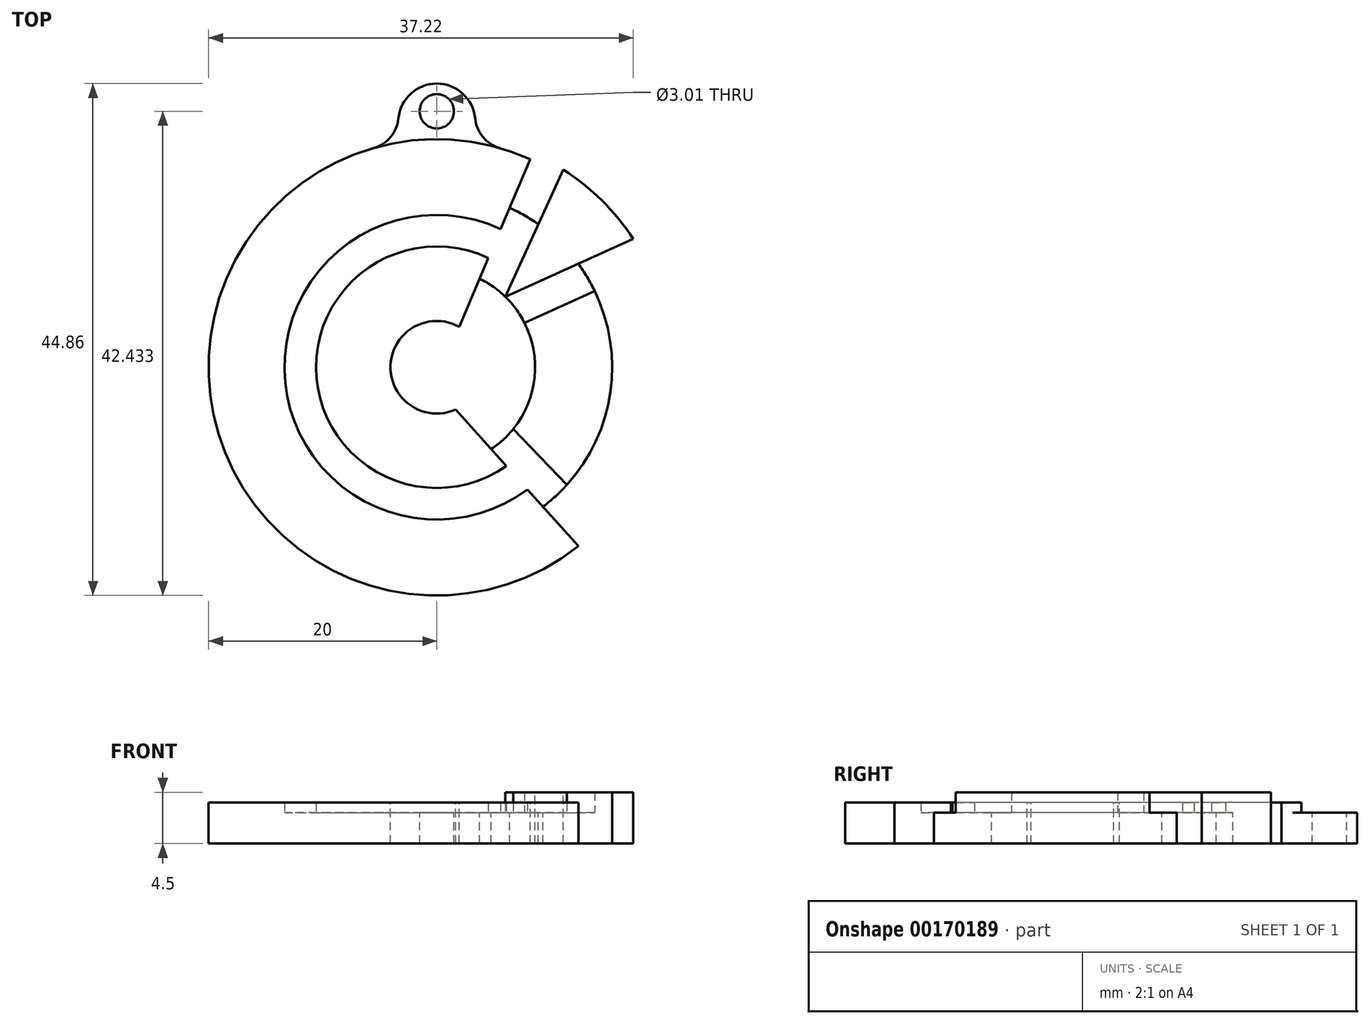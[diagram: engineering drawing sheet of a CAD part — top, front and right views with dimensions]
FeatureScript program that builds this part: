
annotation { "Feature Type Name" : "Feature", "Feature Type Description" : "" }
export const myFeature = defineFeature(function(context is Context, id is Id, definition is map)
    precondition{}
    {
        {
            var Q0;
            Q0=qCreatedBy(makeId("Top.planeOp"),FACE);
            var sketch = newSketch(context, id + "F0", { "sketchPlane" : qUnion([Q0])});
            skCircle(sketch, "E0", {"center": v(0, 0) * mm, "radius": 20 * mm});
            skCircle(sketch, "E1", {"center": v(0, 0) * mm, "radius": 13.35 * mm});
            skCircle(sketch, "E2", {"center": v(0, 0) * mm, "radius": 4.06 * mm});
            skCircle(sketch, "E3", {"center": v(0, 0) * mm, "radius": 10.58 * mm});
            skCircle(sketch, "E4", {"center": v(0, 0) * mm, "radius": 8.61 * mm});
            skCircle(sketch, "E5", {"center": v(0, 0) * mm, "radius": 15.36 * mm});
            skCircle(sketch, "E6", {"center": v(0, 0) * mm, "radius": 20.56 * mm});
            skCircle(sketch, "E7", {"center": v(0, 21.5) * mm, "radius": 3.37 * mm});
            skCircle(sketch, "E8", {"center": v(0, 22.43) * mm, "radius": 1.5 * mm});
            skLineSegment(sketch, "E9", {"start": v(6, 6.18) * mm, "end": v(11.07, 17.32) * mm});
            skLineSegment(sketch, "E10", {"start": v(6, 6.18) * mm, "end": v(17.22, 11.24) * mm});
            skLineSegment(sketch, "E11", {"start": v(8.19, 18.25) * mm, "end": v(1.98, 3.54) * mm});
            skLineSegment(sketch, "E12", {"start": v(1.66, -3.7) * mm, "end": v(12.41, -15.68) * mm});
            skLineSegment(sketch, "E13", {"start": v(7.68, 3.9) * mm, "end": v(13.83, 6.68) * mm});
            skLineSegment(sketch, "E14", {"start": v(11.4, -10.3) * mm, "end": v(6.71, -5.4) * mm});
            skSolve(sketch);
        }
        {
            var Q0;
            {var subQ1=sQuery(id+"F0.wireOp",EDGE,"E0");var subQ4=sQuery(id+"F0.wireOp",EDGE,"E11");var subQ10=makeQuery(id+"F0.imprint","INTERSECT",VERTEX,{"derivedFrom":[subQ1,subQ4]});Q0=makeQuery(id+"F0.imprint","IMPRINT",FACE,{"disambiguationData":[TD([[makeQuery(id+"F0.imprint","IMPRINT",EDGE,{"disambiguationData":[TD([[subQ10,-1.0]])],"derivedFrom":subQ1}),1.0]])]});}
            var Q1;
            {var subQ0=sQuery(id+"F0.wireOp",EDGE,"E11");var subQ1=sQuery(id+"F0.wireOp",EDGE,"E1");var subQ2=makeQuery(id+"F0.imprint","INTERSECT",VERTEX,{"derivedFrom":[subQ1,subQ0]});Q1=makeQuery(id+"F0.imprint","IMPRINT",FACE,{"disambiguationData":[TD([[makeQuery(id+"F0.imprint","IMPRINT",EDGE,{"disambiguationData":[TD([[subQ2,-1.0]])],"derivedFrom":subQ1}),-1.0]])]});}
            var Q2;
            {var subQ0=sQuery(id+"F0.wireOp",EDGE,"E11");var subQ1=sQuery(id+"F0.wireOp",EDGE,"E1");var subQ2=makeQuery(id+"F0.imprint","INTERSECT",VERTEX,{"derivedFrom":[subQ1,subQ0]});Q2=makeQuery(id+"F0.imprint","IMPRINT",FACE,{"disambiguationData":[TD([[makeQuery(id+"F0.imprint","IMPRINT",EDGE,{"disambiguationData":[TD([[subQ2,-1.0]])],"derivedFrom":subQ1}),1.0]])]});}
            var Q3;
            {var subQ0=sQuery(id+"F0.wireOp",EDGE,"E11");var subQ1=sQuery(id+"F0.wireOp",EDGE,"E3");var subQ2=makeQuery(id+"F0.imprint","INTERSECT",VERTEX,{"derivedFrom":[subQ1,subQ0]});Q3=makeQuery(id+"F0.imprint","IMPRINT",FACE,{"disambiguationData":[TD([[makeQuery(id+"F0.imprint","IMPRINT",EDGE,{"disambiguationData":[TD([[subQ2,-1.0]])],"derivedFrom":subQ1}),1.0]])]});}
            var Q4;
            {var subQ0=sQuery(id+"F0.wireOp",EDGE,"E11");var subQ1=sQuery(id+"F0.wireOp",EDGE,"E2");var subQ2=makeQuery(id+"F0.imprint","INTERSECT",VERTEX,{"derivedFrom":[subQ1,subQ0]});Q4=makeQuery(id+"F0.imprint","IMPRINT",FACE,{"disambiguationData":[TD([[makeQuery(id+"F0.imprint","IMPRINT",EDGE,{"disambiguationData":[TD([[subQ2,-1.0]])],"derivedFrom":subQ1}),-1.0]])]});}
            var Q5;
            {var subQ0=sQuery(id+"F0.wireOp",EDGE,"E7");var subQ1=sQuery(id+"F0.wireOp",EDGE,"E0");var subQ2=makeQuery(id+"F0.imprint","INTERSECT",VERTEX,{"disambiguationData":[OD(0.0)],"derivedFrom":[subQ1,subQ0]});Q5=makeQuery(id+"F0.imprint","IMPRINT",FACE,{"disambiguationData":[TD([[makeQuery(id+"F0.imprint","IMPRINT",EDGE,{"disambiguationData":[TD([[subQ2,-1.0]])],"derivedFrom":subQ1}),1.0]])]});}
            var Q6;
            {var subQ0=sQuery(id+"F0.wireOp",EDGE,"E7");var subQ1=sQuery(id+"F0.wireOp",EDGE,"E0");var subQ2=makeQuery(id+"F0.imprint","INTERSECT",VERTEX,{"disambiguationData":[OD(0.0)],"derivedFrom":[subQ1,subQ0]});Q6=makeQuery(id+"F0.imprint","IMPRINT",FACE,{"disambiguationData":[TD([[makeQuery(id+"F0.imprint","IMPRINT",EDGE,{"disambiguationData":[TD([[subQ2,-1.0]])],"derivedFrom":subQ1}),-1.0]])]});}
            var Q7;
            Q7=makeQuery(id+"F0.imprint","IMPRINT",FACE,{"disambiguationData":[TD([[makeQuery(id+"F0.imprint","IMPRINT",EDGE,{"derivedFrom":sQuery(id+"F0.wireOp",EDGE,"E8")}),-1.0]])]});
            var Q8;
            {var subQ0=sQuery(id+"F0.wireOp",EDGE,"E10");var subQ1=sQuery(id+"F0.wireOp",EDGE,"E1");var subQ2=makeQuery(id+"F0.imprint","INTERSECT",VERTEX,{"derivedFrom":[subQ1,subQ0]});Q8=makeQuery(id+"F0.imprint","IMPRINT",FACE,{"disambiguationData":[TD([[makeQuery(id+"F0.imprint","IMPRINT",EDGE,{"disambiguationData":[TD([[subQ2,1.0]])],"derivedFrom":subQ1}),-1.0]])]});}
            var Q9;
            {var subQ0=sQuery(id+"F0.wireOp",EDGE,"E10");var subQ1=sQuery(id+"F0.wireOp",EDGE,"E1");var subQ2=makeQuery(id+"F0.imprint","INTERSECT",VERTEX,{"derivedFrom":[subQ1,subQ0]});Q9=makeQuery(id+"F0.imprint","IMPRINT",FACE,{"disambiguationData":[TD([[makeQuery(id+"F0.imprint","IMPRINT",EDGE,{"disambiguationData":[TD([[subQ2,1.0]])],"derivedFrom":subQ1}),1.0]])]});}
            var Q10;
            {var subQ0=sQuery(id+"F0.wireOp",EDGE,"E10");var subQ1=sQuery(id+"F0.wireOp",EDGE,"E3");var subQ2=makeQuery(id+"F0.imprint","INTERSECT",VERTEX,{"derivedFrom":[subQ1,subQ0]});Q10=makeQuery(id+"F0.imprint","IMPRINT",FACE,{"disambiguationData":[TD([[makeQuery(id+"F0.imprint","IMPRINT",EDGE,{"disambiguationData":[TD([[subQ2,1.0]])],"derivedFrom":subQ1}),1.0]])]});}
            var Q11;
            {var subQ0=sQuery(id+"F0.wireOp",EDGE,"E9");var subQ1=sQuery(id+"F0.wireOp",EDGE,"E3");var subQ2=makeQuery(id+"F0.imprint","INTERSECT",VERTEX,{"derivedFrom":[subQ1,subQ0]});Q11=makeQuery(id+"F0.imprint","IMPRINT",FACE,{"disambiguationData":[TD([[makeQuery(id+"F0.imprint","IMPRINT",EDGE,{"disambiguationData":[TD([[subQ2,1.0]])],"derivedFrom":subQ1}),1.0]])]});}
            var Q12;
            {var subQ0=sQuery(id+"F0.wireOp",EDGE,"E9");var subQ1=sQuery(id+"F0.wireOp",EDGE,"E3");var subQ2=makeQuery(id+"F0.imprint","INTERSECT",VERTEX,{"derivedFrom":[subQ1,subQ0]});Q12=makeQuery(id+"F0.imprint","IMPRINT",FACE,{"disambiguationData":[TD([[makeQuery(id+"F0.imprint","IMPRINT",EDGE,{"disambiguationData":[TD([[subQ2,-1.0]])],"derivedFrom":subQ1}),1.0]])]});}
            var Q13;
            {var subQ0=sQuery(id+"F0.wireOp",EDGE,"E9");var subQ1=sQuery(id+"F0.wireOp",EDGE,"E1");var subQ2=makeQuery(id+"F0.imprint","INTERSECT",VERTEX,{"derivedFrom":[subQ1,subQ0]});Q13=makeQuery(id+"F0.imprint","IMPRINT",FACE,{"disambiguationData":[TD([[makeQuery(id+"F0.imprint","IMPRINT",EDGE,{"disambiguationData":[TD([[subQ2,-1.0]])],"derivedFrom":subQ1}),1.0]])]});}
            var Q14;
            {var subQ0=sQuery(id+"F0.wireOp",EDGE,"E9");var subQ1=sQuery(id+"F0.wireOp",EDGE,"E1");var subQ2=makeQuery(id+"F0.imprint","INTERSECT",VERTEX,{"derivedFrom":[subQ1,subQ0]});Q14=makeQuery(id+"F0.imprint","IMPRINT",FACE,{"disambiguationData":[TD([[makeQuery(id+"F0.imprint","IMPRINT",EDGE,{"disambiguationData":[TD([[subQ2,-1.0]])],"derivedFrom":subQ1}),-1.0]])]});}
            var Q15;
            {var subQ0=sQuery(id+"F0.wireOp",EDGE,"E9");var subQ1=sQuery(id+"F0.wireOp",EDGE,"E1");var subQ2=makeQuery(id+"F0.imprint","INTERSECT",VERTEX,{"derivedFrom":[subQ1,subQ0]});Q15=makeQuery(id+"F0.imprint","IMPRINT",FACE,{"disambiguationData":[TD([[makeQuery(id+"F0.imprint","IMPRINT",EDGE,{"disambiguationData":[TD([[subQ2,1.0]])],"derivedFrom":subQ1}),1.0]])]});}
            var Q16;
            {var subQ0=sQuery(id+"F0.wireOp",EDGE,"E9");var subQ1=sQuery(id+"F0.wireOp",EDGE,"E1");var subQ2=makeQuery(id+"F0.imprint","INTERSECT",VERTEX,{"derivedFrom":[subQ1,subQ0]});Q16=makeQuery(id+"F0.imprint","IMPRINT",FACE,{"disambiguationData":[TD([[makeQuery(id+"F0.imprint","IMPRINT",EDGE,{"disambiguationData":[TD([[subQ2,1.0]])],"derivedFrom":subQ1}),-1.0]])]});}
            var Q17;
            {var subQ0=sQuery(id+"F0.wireOp",EDGE,"E9");var subQ1=sQuery(id+"F0.wireOp",EDGE,"E0");var subQ2=makeQuery(id+"F0.imprint","INTERSECT",VERTEX,{"derivedFrom":[subQ1,subQ0]});Q17=makeQuery(id+"F0.imprint","IMPRINT",FACE,{"disambiguationData":[TD([[makeQuery(id+"F0.imprint","IMPRINT",EDGE,{"disambiguationData":[TD([[subQ2,1.0]])],"derivedFrom":subQ1}),1.0]])]});}
            var Q18;
            {var subQ0=sQuery(id+"F0.wireOp",EDGE,"E9");var subQ1=sQuery(id+"F0.wireOp",EDGE,"E0");var subQ2=makeQuery(id+"F0.imprint","INTERSECT",VERTEX,{"derivedFrom":[subQ1,subQ0]});Q18=makeQuery(id+"F0.imprint","IMPRINT",FACE,{"disambiguationData":[TD([[makeQuery(id+"F0.imprint","IMPRINT",EDGE,{"disambiguationData":[TD([[subQ2,1.0]])],"derivedFrom":subQ1}),-1.0]])]});}
            extrude(context, id + "F1", {"entities" : qUnion([Q0, Q1, Q2, Q3, Q4, Q5, Q6, Q7, Q8, Q9, Q10, Q11, Q12, Q13, Q14, Q15, Q16, Q17, Q18]), "oppositeDirection" : true, "depth" : 2.7 * mm});
        }
        {
            var Q0;
            {var subQ1=sQuery(id+"F0.wireOp",EDGE,"E0");var subQ4=sQuery(id+"F0.wireOp",EDGE,"E11");var subQ10=makeQuery(id+"F0.imprint","INTERSECT",VERTEX,{"derivedFrom":[subQ1,subQ4]});Q0=makeQuery(id+"F0.imprint","IMPRINT",FACE,{"disambiguationData":[TD([[makeQuery(id+"F0.imprint","IMPRINT",EDGE,{"disambiguationData":[TD([[subQ10,-1.0]])],"derivedFrom":subQ1}),1.0]])]});}
            var Q1;
            {var subQ0=sQuery(id+"F0.wireOp",EDGE,"E11");var subQ1=sQuery(id+"F0.wireOp",EDGE,"E1");var subQ2=makeQuery(id+"F0.imprint","INTERSECT",VERTEX,{"derivedFrom":[subQ1,subQ0]});Q1=makeQuery(id+"F0.imprint","IMPRINT",FACE,{"disambiguationData":[TD([[makeQuery(id+"F0.imprint","IMPRINT",EDGE,{"disambiguationData":[TD([[subQ2,-1.0]])],"derivedFrom":subQ1}),-1.0]])]});}
            var Q2;
            {var subQ0=sQuery(id+"F0.wireOp",EDGE,"E11");var subQ1=sQuery(id+"F0.wireOp",EDGE,"E3");var subQ2=makeQuery(id+"F0.imprint","INTERSECT",VERTEX,{"derivedFrom":[subQ1,subQ0]});Q2=makeQuery(id+"F0.imprint","IMPRINT",FACE,{"disambiguationData":[TD([[makeQuery(id+"F0.imprint","IMPRINT",EDGE,{"disambiguationData":[TD([[subQ2,-1.0]])],"derivedFrom":subQ1}),1.0]])]});}
            var Q3;
            {var subQ0=sQuery(id+"F0.wireOp",EDGE,"E11");var subQ1=sQuery(id+"F0.wireOp",EDGE,"E2");var subQ2=makeQuery(id+"F0.imprint","INTERSECT",VERTEX,{"derivedFrom":[subQ1,subQ0]});Q3=makeQuery(id+"F0.imprint","IMPRINT",FACE,{"disambiguationData":[TD([[makeQuery(id+"F0.imprint","IMPRINT",EDGE,{"disambiguationData":[TD([[subQ2,-1.0]])],"derivedFrom":subQ1}),-1.0]])]});}
            var Q4;
            {var subQ0=sQuery(id+"F0.wireOp",EDGE,"E7");var subQ1=sQuery(id+"F0.wireOp",EDGE,"E0");var subQ2=makeQuery(id+"F0.imprint","INTERSECT",VERTEX,{"disambiguationData":[OD(0.0)],"derivedFrom":[subQ1,subQ0]});Q4=makeQuery(id+"F0.imprint","IMPRINT",FACE,{"disambiguationData":[TD([[makeQuery(id+"F0.imprint","IMPRINT",EDGE,{"disambiguationData":[TD([[subQ2,-1.0]])],"derivedFrom":subQ1}),1.0]])]});}
            extrude(context, id + "F2", {"entities" : qUnion([Q0, Q1, Q2, Q3, Q4]), "operationType" : NewBodyOperationType.ADD, "depth" : 0.9 * mm});
        }
        {
            var Q0;
            {var subQ0=sQuery(id+"F0.wireOp",EDGE,"E13");var subQ1=sQuery(id+"F0.wireOp",EDGE,"E3");var subQ2=makeQuery(id+"F0.imprint","INTERSECT",VERTEX,{"derivedFrom":[subQ1,subQ0]});Q0=makeQuery(id+"F0.imprint","IMPRINT",FACE,{"disambiguationData":[TD([[makeQuery(id+"F0.imprint","IMPRINT",EDGE,{"disambiguationData":[TD([[subQ2,1.0]])],"derivedFrom":subQ1}),1.0]])]});}
            var Q1;
            {var subQ0=sQuery(id+"F0.wireOp",EDGE,"E13");var subQ1=sQuery(id+"F0.wireOp",EDGE,"E1");var subQ2=makeQuery(id+"F0.imprint","INTERSECT",VERTEX,{"derivedFrom":[subQ1,subQ0]});Q1=makeQuery(id+"F0.imprint","IMPRINT",FACE,{"disambiguationData":[TD([[makeQuery(id+"F0.imprint","IMPRINT",EDGE,{"disambiguationData":[TD([[subQ2,1.0]])],"derivedFrom":subQ1}),1.0]])]});}
            var Q2;
            {var subQ0=sQuery(id+"F0.wireOp",EDGE,"E13");var subQ1=sQuery(id+"F0.wireOp",EDGE,"E1");var subQ2=makeQuery(id+"F0.imprint","INTERSECT",VERTEX,{"derivedFrom":[subQ1,subQ0]});Q2=makeQuery(id+"F0.imprint","IMPRINT",FACE,{"disambiguationData":[TD([[makeQuery(id+"F0.imprint","IMPRINT",EDGE,{"disambiguationData":[TD([[subQ2,1.0]])],"derivedFrom":subQ1}),-1.0]])]});}
            var Q3;
            {var subQ0=sQuery(id+"F0.wireOp",EDGE,"E12");var subQ1=sQuery(id+"F0.wireOp",EDGE,"E1");var subQ2=makeQuery(id+"F0.imprint","INTERSECT",VERTEX,{"derivedFrom":[subQ1,subQ0]});Q3=makeQuery(id+"F0.imprint","IMPRINT",FACE,{"disambiguationData":[TD([[makeQuery(id+"F0.imprint","IMPRINT",EDGE,{"disambiguationData":[TD([[subQ2,-1.0]])],"derivedFrom":subQ1}),-1.0]])]});}
            var Q4;
            {var subQ0=sQuery(id+"F0.wireOp",EDGE,"E12");var subQ1=sQuery(id+"F0.wireOp",EDGE,"E1");var subQ2=makeQuery(id+"F0.imprint","INTERSECT",VERTEX,{"derivedFrom":[subQ1,subQ0]});Q4=makeQuery(id+"F0.imprint","IMPRINT",FACE,{"disambiguationData":[TD([[makeQuery(id+"F0.imprint","IMPRINT",EDGE,{"disambiguationData":[TD([[subQ2,-1.0]])],"derivedFrom":subQ1}),1.0]])]});}
            var Q5;
            {var subQ0=sQuery(id+"F0.wireOp",EDGE,"E12");var subQ1=sQuery(id+"F0.wireOp",EDGE,"E3");var subQ2=makeQuery(id+"F0.imprint","INTERSECT",VERTEX,{"derivedFrom":[subQ1,subQ0]});Q5=makeQuery(id+"F0.imprint","IMPRINT",FACE,{"disambiguationData":[TD([[makeQuery(id+"F0.imprint","IMPRINT",EDGE,{"disambiguationData":[TD([[subQ2,-1.0]])],"derivedFrom":subQ1}),1.0]])]});}
            extrude(context, id + "F3", {"entities" : qUnion([Q0, Q1, Q2, Q3, Q4, Q5]), "operationType" : NewBodyOperationType.ADD, "oppositeDirection" : true, "depth" : 2.7 * mm});
        }
        {
            var Q0;
            {var subQ0=sQuery(id+"F0.wireOp",EDGE,"E13");var subQ1=sQuery(id+"F0.wireOp",EDGE,"E1");var subQ2=makeQuery(id+"F0.imprint","INTERSECT",VERTEX,{"derivedFrom":[subQ1,subQ0]});Q0=makeQuery(id+"F0.imprint","IMPRINT",FACE,{"disambiguationData":[TD([[makeQuery(id+"F0.imprint","IMPRINT",EDGE,{"disambiguationData":[TD([[subQ2,1.0]])],"derivedFrom":subQ1}),-1.0]])]});}
            var Q1;
            {var subQ0=sQuery(id+"F0.wireOp",EDGE,"E13");var subQ1=sQuery(id+"F0.wireOp",EDGE,"E1");var subQ2=makeQuery(id+"F0.imprint","INTERSECT",VERTEX,{"derivedFrom":[subQ1,subQ0]});Q1=makeQuery(id+"F0.imprint","IMPRINT",FACE,{"disambiguationData":[TD([[makeQuery(id+"F0.imprint","IMPRINT",EDGE,{"disambiguationData":[TD([[subQ2,1.0]])],"derivedFrom":subQ1}),1.0]])]});}
            var Q2;
            {var subQ0=sQuery(id+"F0.wireOp",EDGE,"E13");var subQ1=sQuery(id+"F0.wireOp",EDGE,"E3");var subQ2=makeQuery(id+"F0.imprint","INTERSECT",VERTEX,{"derivedFrom":[subQ1,subQ0]});Q2=makeQuery(id+"F0.imprint","IMPRINT",FACE,{"disambiguationData":[TD([[makeQuery(id+"F0.imprint","IMPRINT",EDGE,{"disambiguationData":[TD([[subQ2,1.0]])],"derivedFrom":subQ1}),1.0]])]});}
            var Q3;
            {var subQ0=sQuery(id+"F0.wireOp",EDGE,"E9");var subQ1=sQuery(id+"F0.wireOp",EDGE,"E0");var subQ2=makeQuery(id+"F0.imprint","INTERSECT",VERTEX,{"derivedFrom":[subQ1,subQ0]});Q3=makeQuery(id+"F0.imprint","IMPRINT",FACE,{"disambiguationData":[TD([[makeQuery(id+"F0.imprint","IMPRINT",EDGE,{"disambiguationData":[TD([[subQ2,1.0]])],"derivedFrom":subQ1}),-1.0]])]});}
            var Q4;
            {var subQ0=sQuery(id+"F0.wireOp",EDGE,"E10");var subQ1=sQuery(id+"F0.wireOp",EDGE,"E3");var subQ2=makeQuery(id+"F0.imprint","INTERSECT",VERTEX,{"derivedFrom":[subQ1,subQ0]});Q4=makeQuery(id+"F0.imprint","IMPRINT",FACE,{"disambiguationData":[TD([[makeQuery(id+"F0.imprint","IMPRINT",EDGE,{"disambiguationData":[TD([[subQ2,-1.0]])],"derivedFrom":subQ1}),1.0]])]});}
            var Q5;
            {var subQ0=sQuery(id+"F0.wireOp",EDGE,"E10");var subQ1=sQuery(id+"F0.wireOp",EDGE,"E1");var subQ2=makeQuery(id+"F0.imprint","INTERSECT",VERTEX,{"derivedFrom":[subQ1,subQ0]});Q5=makeQuery(id+"F0.imprint","IMPRINT",FACE,{"disambiguationData":[TD([[makeQuery(id+"F0.imprint","IMPRINT",EDGE,{"disambiguationData":[TD([[subQ2,-1.0]])],"derivedFrom":subQ1}),1.0]])]});}
            var Q6;
            {var subQ0=sQuery(id+"F0.wireOp",EDGE,"E10");var subQ1=sQuery(id+"F0.wireOp",EDGE,"E1");var subQ2=makeQuery(id+"F0.imprint","INTERSECT",VERTEX,{"derivedFrom":[subQ1,subQ0]});Q6=makeQuery(id+"F0.imprint","IMPRINT",FACE,{"disambiguationData":[TD([[makeQuery(id+"F0.imprint","IMPRINT",EDGE,{"disambiguationData":[TD([[subQ2,-1.0]])],"derivedFrom":subQ1}),-1.0]])]});}
            var Q7;
            {var subQ0=sQuery(id+"F0.wireOp",EDGE,"E9");var subQ1=sQuery(id+"F0.wireOp",EDGE,"E0");var subQ2=makeQuery(id+"F0.imprint","INTERSECT",VERTEX,{"derivedFrom":[subQ1,subQ0]});Q7=makeQuery(id+"F0.imprint","IMPRINT",FACE,{"disambiguationData":[TD([[makeQuery(id+"F0.imprint","IMPRINT",EDGE,{"disambiguationData":[TD([[subQ2,1.0]])],"derivedFrom":subQ1}),1.0]])]});}
            extrude(context, id + "F4", {"entities" : qUnion([Q0, Q1, Q2, Q3, Q4, Q5, Q6, Q7]), "operationType" : NewBodyOperationType.ADD, "depth" : 1.8 * mm});
        }
        {
            var Q0;
            {var subQ0=sQuery(id+"F0.wireOp",EDGE,"E7");var subQ1=sQuery(id+"F0.wireOp",EDGE,"E0");Q0=makeQuery(id+"F1.opExtrude","SWEPT_EDGE",EDGE,{"disambiguationData":[OSD([subQ1,subQ0]),TDD([makeQuery(id+"F0.imprint","INTERSECT",VERTEX,{"disambiguationData":[OD(0.0)],"derivedFrom":[subQ1,subQ0]})])]});}
            var Q1;
            {var subQ0=sQuery(id+"F0.wireOp",EDGE,"E7");var subQ1=sQuery(id+"F0.wireOp",EDGE,"E0");Q1=makeQuery(id+"F1.opExtrude","SWEPT_EDGE",EDGE,{"disambiguationData":[OSD([subQ1,subQ0]),TDD([makeQuery(id+"F0.imprint","INTERSECT",VERTEX,{"disambiguationData":[OD(1.0)],"derivedFrom":[subQ1,subQ0]})])]});}
            fillet(context, id + "F5", {"entities" : qUnion([Q0, Q1]), "radius" : 3 * mm, "tangentPropagation" : true, "allowEdgeOverflow" : false});
        }
    });
